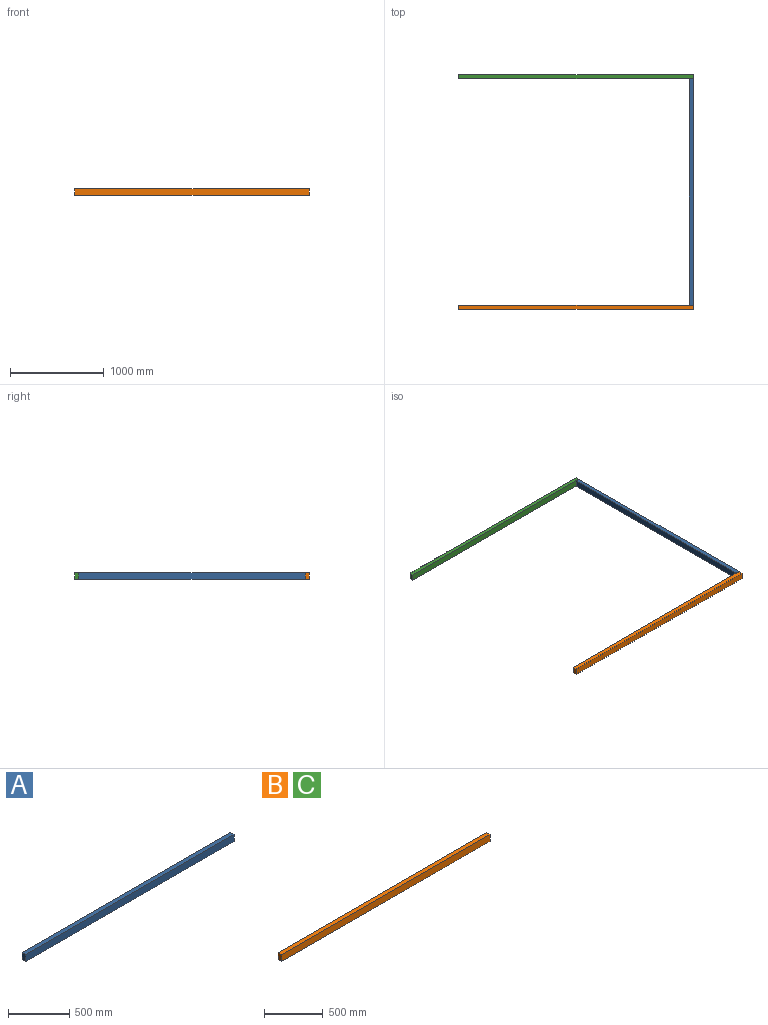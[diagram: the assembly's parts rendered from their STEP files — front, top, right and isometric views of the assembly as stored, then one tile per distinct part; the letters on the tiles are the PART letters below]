
ASSEMBLY  parts=3 mates=1
PART A: 6 faces, bbox 2410x45x70 mm
  f0: plane 2410x45mm, normal (0,0,1), area 108450mm2, adj f1,f3,f4,f5
  f1: plane 2410x70mm, normal (0,-1,0), area 168700mm2, adj f0,f2,f4,f5
  f2: plane 2410x45mm, normal (0,0,-1), area 108450mm2, adj f1,f3,f4,f5
  f3: plane 2410x70mm, normal (0,1,0), area 168700mm2, adj f0,f2,f4,f5
  f4: plane 70x45mm, normal (1,0,0), area 3150mm2, adj f0,f1,f2,f3
  f5: plane 70x45mm, normal (-1,0,0), area 3150mm2, adj f0,f1,f2,f3
PART B: 6 faces, bbox 2500x45x70 mm
  f0: plane 2500x45mm, normal (0,0,1), area 112500mm2, adj f1,f3,f4,f5
  f1: plane 2500x70mm, normal (0,-1,0), area 175000mm2, adj f0,f2,f4,f5
  f2: plane 2500x45mm, normal (0,0,-1), area 112500mm2, adj f1,f3,f4,f5
  f3: plane 2500x70mm, normal (0,1,0), area 175000mm2, adj f0,f2,f4,f5
  f4: plane 70x45mm, normal (1,0,0), area 3150mm2, adj f0,f1,f2,f3
  f5: plane 70x45mm, normal (-1,0,0), area 3150mm2, adj f0,f1,f2,f3
PART C: same geometry as B
PLACE A rot(axis=(0,0,-1),90deg) t=(1662.7,2494.4,-318.75)mm
PLACE B t=(-829.05,76.15,-318.75)mm
PLACE C t=(-829.05,2531.15,-318.75)mm
MATE fastened A.f4 <-> B.f3  axis (0,-1,0) through (1670.95,84.4,-236.71)mm
